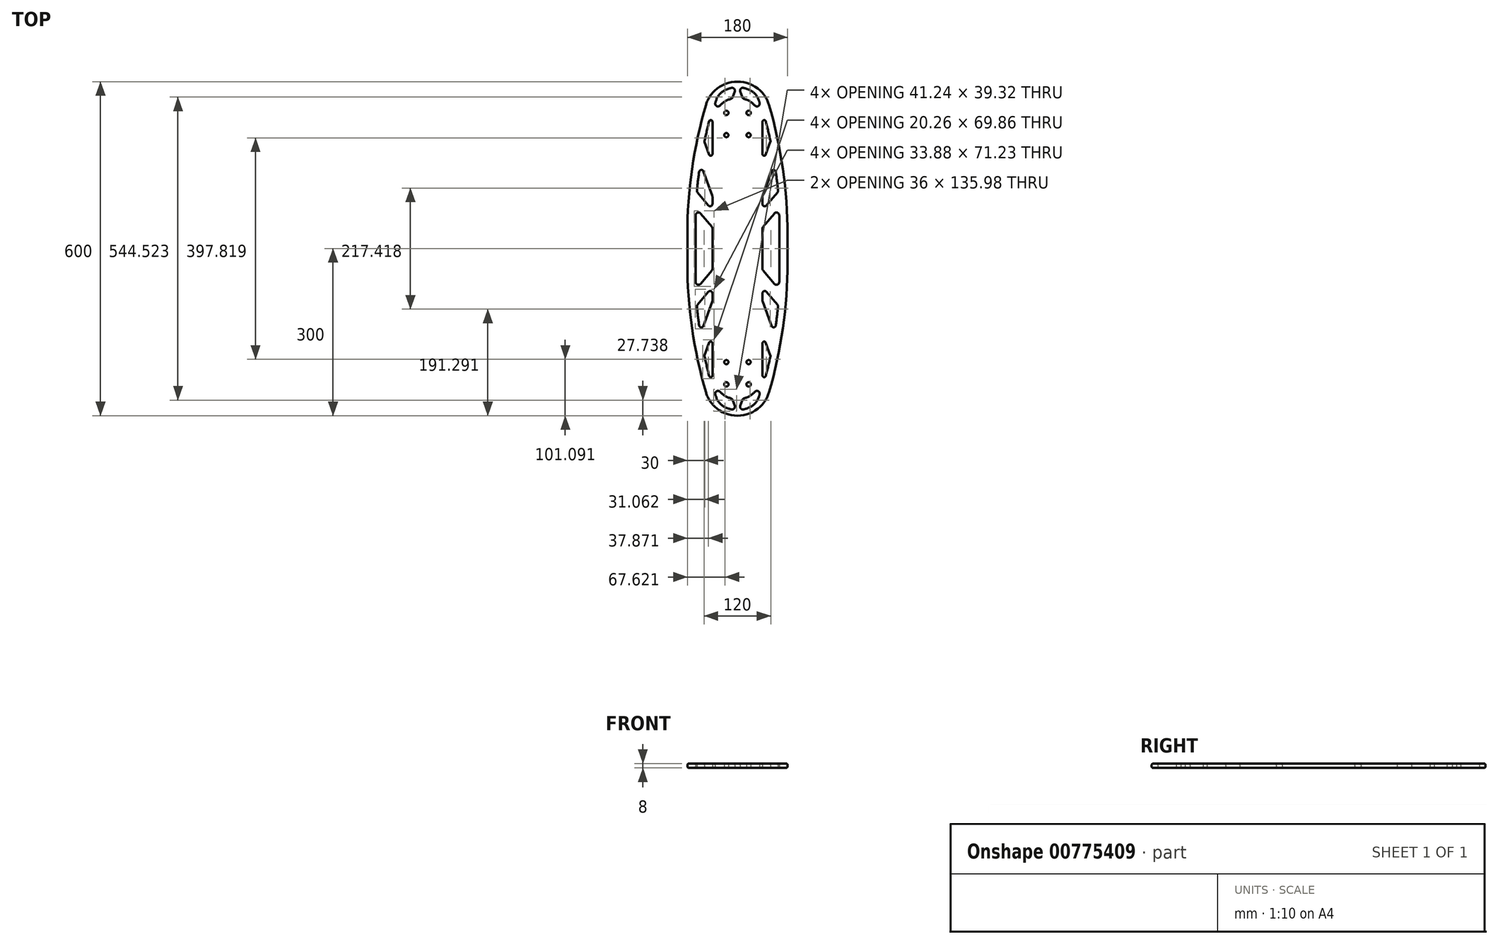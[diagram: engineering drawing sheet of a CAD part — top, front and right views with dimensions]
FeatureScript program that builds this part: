
annotation { "Feature Type Name" : "Feature", "Feature Type Description" : "" }
export const myFeature = defineFeature(function(context is Context, id is Id, definition is map)
    precondition{}
    {
        {
            var Q0;
            Q0=qCreatedBy(makeId("Top.planeOp"),FACE);
            var sketch = newSketch(context, id + "F0", { "sketchPlane" : qUnion([Q0])});
            skLineSegment(sketch, "E0", {"start": v(0, 0) * mm, "end": v(0, 300) * mm});
            skLineSegment(sketch, "E1", {"start": v(0, 0) * mm, "end": v(-45, 0) * mm});
            skLineSegment(sketch, "E2", {"start": v(-90, 0) * mm, "end": v(-90, 25) * mm});
            skArc(sketch, "E3", {"start": v(-56.38, 258.83) * mm, "mid": v(-81.55, 143.12) * mm, "end": v(-90, 25) * mm});
            skArc(sketch, "E4.trimOffspring", {"start": v(0, 300) * mm, "mid": v(-22.04, 295.8) * mm, "end": v(-41, 283.81) * mm});
            skArc(sketch, "E5.filletArc", {"start": v(-41, 283.81) * mm, "mid": v(-50.36, 272.35) * mm, "end": v(-56.38, 258.83) * mm});
            skLineSegment(sketch, "E6", {"start": v(-75, 60) * mm, "end": v(-75, 0) * mm});
            skLineSegment(sketch, "E7", {"start": v(-45, 0) * mm, "end": v(-45, 36.56) * mm});
            skArc(sketch, "E8.trimOffspring", {"start": v(-50.9, 228.63) * mm, "mid": v(-55.25, 210.96) * mm, "end": v(-59.2, 193.2) * mm});
            skArc(sketch, "E9", {"start": v(-38.47, 266.28) * mm, "mid": v(-39.13, 264.12) * mm, "end": v(-39.8, 261.96) * mm});
            skArc(sketch, "E10", {"start": v(-11.7, 269.12) * mm, "mid": v(-22.35, 264.46) * mm, "end": v(-31.35, 257.1) * mm});
            skArc(sketch, "E11.trimOffspring", {"start": v(-10.83, 288.81) * mm, "mid": v(-17.8, 286.72) * mm, "end": v(-24.41, 283.64) * mm});
            skLineSegment(sketch, "E12.trimOffspring", {"start": v(-75, 0) * mm, "end": v(-90, 0) * mm});
            skLineSegment(sketch, "E13", {"start": v(0, 0) * mm, "end": v(-74.24, 88.36) * mm, "construction": true});
            skLineSegment(sketch, "E14", {"start": v(0, 0) * mm, "end": v(-63.1, 173.38) * mm, "construction": true});
            skLineSegment(sketch, "E15", {"start": v(-59.08, 191.55) * mm, "end": v(-50.82, 168.86) * mm});
            skLineSegment(sketch, "E16", {"start": v(-61.14, 138.73) * mm, "end": v(-45.24, 95.06) * mm});
            skArc(sketch, "E17.trimOffspring", {"start": v(-68.86, 137.92) * mm, "mid": v(-71.03, 121.05) * mm, "end": v(-72.86, 104.13) * mm});
            skLineSegment(sketch, "E18.trimOffspring", {"start": v(-45, 169.89) * mm, "end": v(-45, 227.89) * mm});
            skLineSegment(sketch, "E19", {"start": v(-71.94, 101.17) * mm, "end": v(-52.06, 77.51) * mm});
            skLineSegment(sketch, "E20", {"start": v(-66.17, 63.22) * mm, "end": v(-45.94, 39.13) * mm});
            skLineSegment(sketch, "E21.trimOffspring", {"start": v(-45, 80.09) * mm, "end": v(-45, 93.7) * mm});
            skArc(sketch, "E22.filletArc", {"start": v(-45, 227.89) * mm, "mid": v(-47.62, 230.86) * mm, "end": v(-50.9, 228.63) * mm});
            skPoint(sketch, "E23.visualSharp", {"position": v(-59.37, 192.35) * mm});
            skArc(sketch, "E23.filletArc", {"start": v(-59.2, 193.2) * mm, "mid": v(-59.25, 192.36) * mm, "end": v(-59.08, 191.55) * mm});
            skPoint(sketch, "E24.visualSharp", {"position": v(-45, 152.87) * mm});
            skArc(sketch, "E24.filletArc", {"start": v(-50.82, 168.86) * mm, "mid": v(-47.48, 166.93) * mm, "end": v(-45, 169.89) * mm});
            skPoint(sketch, "E25.visualSharp", {"position": v(-66.52, 153.53) * mm});
            skArc(sketch, "E25.filletArc", {"start": v(-61.14, 138.73) * mm, "mid": v(-65.31, 141.34) * mm, "end": v(-68.86, 137.92) * mm});
            skPoint(sketch, "E26.visualSharp", {"position": v(-45, 94.4) * mm});
            skArc(sketch, "E26.filletArc", {"start": v(-45, 93.7) * mm, "mid": v(-45.06, 94.39) * mm, "end": v(-45.24, 95.06) * mm});
            skPoint(sketch, "E27.visualSharp", {"position": v(-45, 69.1) * mm});
            skArc(sketch, "E27.filletArc", {"start": v(-52.06, 77.51) * mm, "mid": v(-47.63, 76.33) * mm, "end": v(-45, 80.09) * mm});
            skPoint(sketch, "E28.visualSharp", {"position": v(-73.02, 102.46) * mm});
            skArc(sketch, "E28.filletArc", {"start": v(-72.86, 104.13) * mm, "mid": v(-72.7, 102.56) * mm, "end": v(-71.94, 101.17) * mm});
            skPoint(sketch, "E29.visualSharp", {"position": v(-45, 38.02) * mm});
            skArc(sketch, "E29.filletArc", {"start": v(-45, 36.56) * mm, "mid": v(-45.24, 37.93) * mm, "end": v(-45.94, 39.13) * mm});
            skArc(sketch, "E30", {"start": v(-66.17, 63.22) * mm, "mid": v(-71.71, 64.7) * mm, "end": v(-75, 60) * mm});
            skArc(sketch, "E31", {"start": v(-72.86, 104.13) * mm, "mid": v(-74.46, 82.1) * mm, "end": v(-75, 60) * mm, "construction": true});
            skArc(sketch, "E32.filletArc", {"start": v(-24.41, 283.64) * mm, "mid": v(-33.1, 276.3) * mm, "end": v(-38.47, 266.28) * mm});
            skArc(sketch, "E33", {"start": v(-39.8, 261.96) * mm, "mid": v(-37.5, 256.18) * mm, "end": v(-31.35, 257.1) * mm});
            skCircle(sketch, "E34", {"center": v(-20, 243.93) * mm, "radius": 3.89 * mm});
            skCircle(sketch, "E35", {"center": v(-20, 203.93) * mm, "radius": 3.71 * mm});
            skLineSegment(sketch, "E36", {"start": v(-20, 243.93) * mm, "end": v(-20, 203.93) * mm, "construction": true});
            skLineSegment(sketch, "E37", {"start": v(-5, 282.35) * mm, "end": v(-8.33, 272.35) * mm});
            skPoint(sketch, "E38.visualSharp", {"position": v(-2.47, 289.94) * mm});
            skArc(sketch, "E38.filletArc", {"start": v(-5, 282.35) * mm, "mid": v(-6.03, 287.28) * mm, "end": v(-10.83, 288.81) * mm});
            skPoint(sketch, "E39.visualSharp", {"position": v(-9.2, 269.76) * mm});
            skArc(sketch, "E39.filletArc", {"start": v(-11.7, 269.12) * mm, "mid": v(-9.62, 270.32) * mm, "end": v(-8.33, 272.35) * mm});
            skSolve(sketch);
        }
        {
            var Q0;
            Q0=makeQuery(id+"F0.imprint","IMPRINT",FACE,{"disambiguationData":[TD([[makeQuery(id+"F0.imprint","IMPRINT",EDGE,{"derivedFrom":sQuery(id+"F0.wireOp",EDGE,"E0")}),1.0]])]});
            extrude(context, id + "F1", {"entities" : qUnion([Q0]), "depth" : 8 * mm, "offsetDistance" : 25 * mm});
        }
        {
            var Q0;
            Q0=makeQuery(id+"F1.opExtrude","SWEPT_FACE",FACE,{"disambiguationData":[OSD([sQuery(id+"F0.wireOp",EDGE,"E25.filletArc")])]});
            var Q1;
            Q1=makeQuery(id+"F1.opExtrude","SWEPT_FACE",FACE,{"disambiguationData":[OSD([sQuery(id+"F0.wireOp",EDGE,"E22.filletArc")])]});
            var Q2;
            Q2=makeQuery(id+"F1.opExtrude","SWEPT_FACE",FACE,{"disambiguationData":[OSD([sQuery(id+"F0.wireOp",EDGE,"E30")])]});
            var Q3;
            Q3=makeQuery(id+"F1.opExtrude","SWEPT_FACE",FACE,{"disambiguationData":[OSD([sQuery(id+"F0.wireOp",EDGE,"E3")])]});
            var Q4;
            Q4=makeQuery(id+"F1.opExtrude","SWEPT_FACE",FACE,{"disambiguationData":[OSD([sQuery(id+"F0.wireOp",EDGE,"E33")])]});
            fillet(context, id + "F2", {"entities" : qUnion([Q0, Q1, Q2, Q3, Q4]), "radius" : 3 * mm, "tangentPropagation" : true, "allowEdgeOverflow" : false});
        }
        {
            var Q0;
            Q0=makeQuery(id+"F1.opExtrude","SWEPT_BODY",BODY,{"disambiguationData":[OSD([sQuery(id+"F0.wireOp",EDGE,"E0"),sQuery(id+"F0.wireOp",EDGE,"E1"),sQuery(id+"F0.wireOp",EDGE,"E2"),sQuery(id+"F0.wireOp",EDGE,"E3"),sQuery(id+"F0.wireOp",EDGE,"E4.trimOffspring"),sQuery(id+"F0.wireOp",EDGE,"E5.filletArc")])]});
            var Q1;
            Q1=makeQuery(id+"F1.opExtrude","SWEPT_FACE",FACE,{"disambiguationData":[OSD([sQuery(id+"F0.wireOp",EDGE,"E0")])]});
            mirror(context, id + "F3", {"operationType" : NewBodyOperationType.ADD, "entities" : qUnion([Q0]), "mirrorPlane" : qUnion([Q1])});
        }
        {
            var Q0;
            Q0=makeQuery(id+"F1.opExtrude","SWEPT_BODY",BODY,{"disambiguationData":[OSD([sQuery(id+"F0.wireOp",EDGE,"E0"),sQuery(id+"F0.wireOp",EDGE,"E1"),sQuery(id+"F0.wireOp",EDGE,"E2"),sQuery(id+"F0.wireOp",EDGE,"E3"),sQuery(id+"F0.wireOp",EDGE,"E4.trimOffspring"),sQuery(id+"F0.wireOp",EDGE,"E5.filletArc")])]});
            var Q1;
            {var subQ0=makeQuery(id+"F1.opExtrude","SWEPT_FACE",FACE,{"disambiguationData":[OSD([sQuery(id+"F0.wireOp",EDGE,"E1")])]});Q1=makeQuery(id+"F3.boolean.opBoolean","MERGE",FACE,{"derivedFrom":[subQ0,makeQuery(id+"F3.opPattern","COPY",FACE,{"derivedFrom":subQ0,"instanceName":"1"})]});}
            mirror(context, id + "F4", {"operationType" : NewBodyOperationType.ADD, "entities" : qUnion([Q0]), "mirrorPlane" : qUnion([Q1])});
        }
    });
